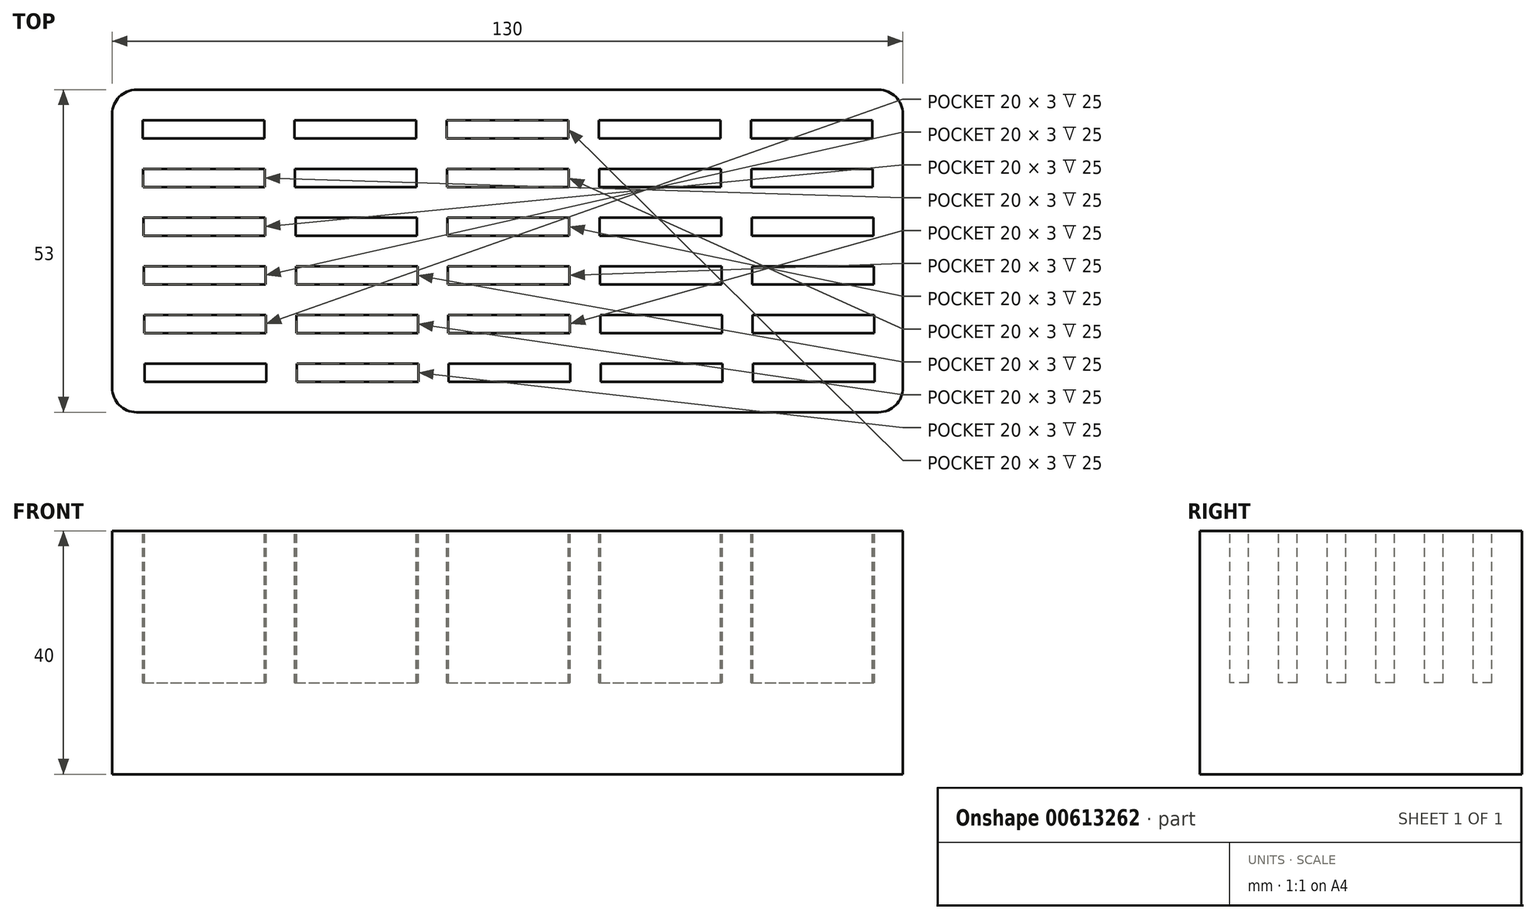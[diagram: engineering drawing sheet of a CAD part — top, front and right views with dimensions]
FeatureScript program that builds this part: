
annotation { "Feature Type Name" : "Feature", "Feature Type Description" : "" }
export const myFeature = defineFeature(function(context is Context, id is Id, definition is map)
    precondition{}
    {
        {
            var Q0;
            Q0=qCreatedBy(makeId("Top.planeOp"),FACE);
            var sketch = newSketch(context, id + "F0", { "sketchPlane" : qUnion([Q0])});
            skLineSegment(sketch, "E0.bottom", {"start": v(4, 0) * mm, "end": v(126, 0) * mm});
            skLineSegment(sketch, "E0.top", {"start": v(4, 53) * mm, "end": v(126, 53) * mm});
            skLineSegment(sketch, "E0.left", {"start": v(0, 4) * mm, "end": v(0, 49) * mm});
            skLineSegment(sketch, "E0.right", {"start": v(130, 4) * mm, "end": v(130, 49) * mm});
            skPoint(sketch, "E1.visualSharp", {"position": v(0, 53) * mm});
            skArc(sketch, "E1.filletArc", {"start": v(4, 53) * mm, "mid": v(1.17, 51.83) * mm, "end": v(0, 49) * mm});
            skPoint(sketch, "E2.visualSharp", {"position": v(0, 0) * mm});
            skArc(sketch, "E2.filletArc", {"start": v(0, 4) * mm, "mid": v(1.17, 1.17) * mm, "end": v(4, 0) * mm});
            skPoint(sketch, "E3.visualSharp", {"position": v(130, 0) * mm});
            skArc(sketch, "E3.filletArc", {"start": v(126, 0) * mm, "mid": v(128.83, 1.17) * mm, "end": v(130, 4) * mm});
            skPoint(sketch, "E4.visualSharp", {"position": v(130, 53) * mm});
            skArc(sketch, "E4.filletArc", {"start": v(130, 49) * mm, "mid": v(128.83, 51.83) * mm, "end": v(126, 53) * mm});
            skSolve(sketch);
        }
        {
            var Q0;
            Q0 = qSketchRegion(id + "F0", true);
            extrude(context, id + "F1", {"entities" : qUnion([Q0]), "depth" : 40 * mm, "offsetDistance" : 25.4 * mm});
        }
        {
            var Q0;
            Q0=makeQuery(id+"F1.opExtrude","CAP_FACE",FACE,{"disambiguationData":[OSD([sQuery(id+"F0.wireOp",EDGE,"E0.bottom"),sQuery(id+"F0.wireOp",EDGE,"E0.top"),sQuery(id+"F0.wireOp",EDGE,"E0.left"),sQuery(id+"F0.wireOp",EDGE,"E0.right"),sQuery(id+"F0.wireOp",EDGE,"E1.filletArc"),sQuery(id+"F0.wireOp",EDGE,"E2.filletArc"),sQuery(id+"F0.wireOp",EDGE,"E3.filletArc"),sQuery(id+"F0.wireOp",EDGE,"E4.filletArc")])],"isStart":false});
            var sketch = newSketch(context, id + "F2", { "sketchPlane" : qUnion([Q0])});
            skLineSegment(sketch, "E5.bottom", {"start": v(5, 48) * mm, "end": v(25, 48) * mm});
            skLineSegment(sketch, "E5.top", {"start": v(5, 45) * mm, "end": v(25, 45) * mm});
            skLineSegment(sketch, "E5.left", {"start": v(5, 48) * mm, "end": v(5, 45) * mm});
            skLineSegment(sketch, "E5.right", {"start": v(25, 48) * mm, "end": v(25, 45) * mm});
            skLineSegment(sketch, "E6.0.1.0", {"start": v(5.07, 37) * mm, "end": v(25.07, 37) * mm});
            skLineSegment(sketch, "E6.0.1.1", {"start": v(5.07, 40) * mm, "end": v(25.07, 40) * mm});
            skLineSegment(sketch, "E6.0.1.2", {"start": v(25.07, 40) * mm, "end": v(25.07, 37) * mm});
            skLineSegment(sketch, "E6.0.1.3", {"start": v(5.07, 40) * mm, "end": v(5.07, 37) * mm});
            skLineSegment(sketch, "E6.0.2.0", {"start": v(5.13, 29) * mm, "end": v(25.13, 29) * mm});
            skLineSegment(sketch, "E6.0.2.1", {"start": v(5.13, 32) * mm, "end": v(25.13, 32) * mm});
            skLineSegment(sketch, "E6.0.2.2", {"start": v(25.13, 32) * mm, "end": v(25.13, 29) * mm});
            skLineSegment(sketch, "E6.0.2.3", {"start": v(5.13, 32) * mm, "end": v(5.13, 29) * mm});
            skLineSegment(sketch, "E6.0.3.0", {"start": v(5.2, 21) * mm, "end": v(25.2, 21) * mm});
            skLineSegment(sketch, "E6.0.3.1", {"start": v(5.2, 24) * mm, "end": v(25.2, 24) * mm});
            skLineSegment(sketch, "E6.0.3.2", {"start": v(25.2, 24) * mm, "end": v(25.2, 21) * mm});
            skLineSegment(sketch, "E6.0.3.3", {"start": v(5.2, 24) * mm, "end": v(5.2, 21) * mm});
            skLineSegment(sketch, "E6.0.4.0", {"start": v(5.27, 13) * mm, "end": v(25.27, 13) * mm});
            skLineSegment(sketch, "E6.0.4.1", {"start": v(5.27, 16) * mm, "end": v(25.27, 16) * mm});
            skLineSegment(sketch, "E6.0.4.2", {"start": v(25.27, 16) * mm, "end": v(25.27, 13) * mm});
            skLineSegment(sketch, "E6.0.4.3", {"start": v(5.27, 16) * mm, "end": v(5.27, 13) * mm});
            skLineSegment(sketch, "E6.0.5.0", {"start": v(5.33, 5) * mm, "end": v(25.33, 5) * mm});
            skLineSegment(sketch, "E6.0.5.1", {"start": v(5.33, 8) * mm, "end": v(25.33, 8) * mm});
            skLineSegment(sketch, "E6.0.5.2", {"start": v(25.33, 8) * mm, "end": v(25.33, 5) * mm});
            skLineSegment(sketch, "E6.0.5.3", {"start": v(5.33, 8) * mm, "end": v(5.33, 5) * mm});
            skLineSegment(sketch, "E6.1.0.0", {"start": v(30, 45) * mm, "end": v(50, 45) * mm});
            skLineSegment(sketch, "E6.1.0.1", {"start": v(30, 48) * mm, "end": v(50, 48) * mm});
            skLineSegment(sketch, "E6.1.0.2", {"start": v(50, 48) * mm, "end": v(50, 45) * mm});
            skLineSegment(sketch, "E6.1.0.3", {"start": v(30, 48) * mm, "end": v(30, 45) * mm});
            skLineSegment(sketch, "E6.1.1.0", {"start": v(30.07, 37) * mm, "end": v(50.07, 37) * mm});
            skLineSegment(sketch, "E6.1.1.1", {"start": v(30.07, 40) * mm, "end": v(50.07, 40) * mm});
            skLineSegment(sketch, "E6.1.1.2", {"start": v(50.07, 40) * mm, "end": v(50.07, 37) * mm});
            skLineSegment(sketch, "E6.1.1.3", {"start": v(30.07, 40) * mm, "end": v(30.07, 37) * mm});
            skLineSegment(sketch, "E6.1.2.0", {"start": v(30.13, 29) * mm, "end": v(50.13, 29) * mm});
            skLineSegment(sketch, "E6.1.2.1", {"start": v(30.13, 32) * mm, "end": v(50.13, 32) * mm});
            skLineSegment(sketch, "E6.1.2.2", {"start": v(50.13, 32) * mm, "end": v(50.13, 29) * mm});
            skLineSegment(sketch, "E6.1.2.3", {"start": v(30.13, 32) * mm, "end": v(30.13, 29) * mm});
            skLineSegment(sketch, "E6.1.3.0", {"start": v(30.2, 21) * mm, "end": v(50.2, 21) * mm});
            skLineSegment(sketch, "E6.1.3.1", {"start": v(30.2, 24) * mm, "end": v(50.2, 24) * mm});
            skLineSegment(sketch, "E6.1.3.2", {"start": v(50.2, 24) * mm, "end": v(50.2, 21) * mm});
            skLineSegment(sketch, "E6.1.3.3", {"start": v(30.2, 24) * mm, "end": v(30.2, 21) * mm});
            skLineSegment(sketch, "E6.1.4.0", {"start": v(30.27, 13) * mm, "end": v(50.27, 13) * mm});
            skLineSegment(sketch, "E6.1.4.1", {"start": v(30.27, 16) * mm, "end": v(50.27, 16) * mm});
            skLineSegment(sketch, "E6.1.4.2", {"start": v(50.27, 16) * mm, "end": v(50.27, 13) * mm});
            skLineSegment(sketch, "E6.1.4.3", {"start": v(30.27, 16) * mm, "end": v(30.27, 13) * mm});
            skLineSegment(sketch, "E6.1.5.0", {"start": v(30.33, 5) * mm, "end": v(50.33, 5) * mm});
            skLineSegment(sketch, "E6.1.5.1", {"start": v(30.33, 8) * mm, "end": v(50.33, 8) * mm});
            skLineSegment(sketch, "E6.1.5.2", {"start": v(50.33, 8) * mm, "end": v(50.33, 5) * mm});
            skLineSegment(sketch, "E6.1.5.3", {"start": v(30.33, 8) * mm, "end": v(30.33, 5) * mm});
            skLineSegment(sketch, "E6.2.0.0", {"start": v(55, 45) * mm, "end": v(75, 45) * mm});
            skLineSegment(sketch, "E6.2.0.1", {"start": v(55, 48) * mm, "end": v(75, 48) * mm});
            skLineSegment(sketch, "E6.2.0.2", {"start": v(75, 48) * mm, "end": v(75, 45) * mm});
            skLineSegment(sketch, "E6.2.0.3", {"start": v(55, 48) * mm, "end": v(55, 45) * mm});
            skLineSegment(sketch, "E6.2.1.0", {"start": v(55.07, 37) * mm, "end": v(75.07, 37) * mm});
            skLineSegment(sketch, "E6.2.1.1", {"start": v(55.07, 40) * mm, "end": v(75.07, 40) * mm});
            skLineSegment(sketch, "E6.2.1.2", {"start": v(75.07, 40) * mm, "end": v(75.07, 37) * mm});
            skLineSegment(sketch, "E6.2.1.3", {"start": v(55.07, 40) * mm, "end": v(55.07, 37) * mm});
            skLineSegment(sketch, "E6.2.2.0", {"start": v(55.13, 29) * mm, "end": v(75.13, 29) * mm});
            skLineSegment(sketch, "E6.2.2.1", {"start": v(55.13, 32) * mm, "end": v(75.13, 32) * mm});
            skLineSegment(sketch, "E6.2.2.2", {"start": v(75.13, 32) * mm, "end": v(75.13, 29) * mm});
            skLineSegment(sketch, "E6.2.2.3", {"start": v(55.13, 32) * mm, "end": v(55.13, 29) * mm});
            skLineSegment(sketch, "E6.2.3.0", {"start": v(55.2, 21) * mm, "end": v(75.2, 21) * mm});
            skLineSegment(sketch, "E6.2.3.1", {"start": v(55.2, 24) * mm, "end": v(75.2, 24) * mm});
            skLineSegment(sketch, "E6.2.3.2", {"start": v(75.2, 24) * mm, "end": v(75.2, 21) * mm});
            skLineSegment(sketch, "E6.2.3.3", {"start": v(55.2, 24) * mm, "end": v(55.2, 21) * mm});
            skLineSegment(sketch, "E6.2.4.0", {"start": v(55.27, 13) * mm, "end": v(75.27, 13) * mm});
            skLineSegment(sketch, "E6.2.4.1", {"start": v(55.27, 16) * mm, "end": v(75.27, 16) * mm});
            skLineSegment(sketch, "E6.2.4.2", {"start": v(75.27, 16) * mm, "end": v(75.27, 13) * mm});
            skLineSegment(sketch, "E6.2.4.3", {"start": v(55.27, 16) * mm, "end": v(55.27, 13) * mm});
            skLineSegment(sketch, "E6.2.5.0", {"start": v(55.33, 5) * mm, "end": v(75.33, 5) * mm});
            skLineSegment(sketch, "E6.2.5.1", {"start": v(55.33, 8) * mm, "end": v(75.33, 8) * mm});
            skLineSegment(sketch, "E6.2.5.2", {"start": v(75.33, 8) * mm, "end": v(75.33, 5) * mm});
            skLineSegment(sketch, "E6.2.5.3", {"start": v(55.33, 8) * mm, "end": v(55.33, 5) * mm});
            skLineSegment(sketch, "E6.3.0.0", {"start": v(80, 45) * mm, "end": v(100, 45) * mm});
            skLineSegment(sketch, "E6.3.0.1", {"start": v(80, 48) * mm, "end": v(100, 48) * mm});
            skLineSegment(sketch, "E6.3.0.2", {"start": v(100, 48) * mm, "end": v(100, 45) * mm});
            skLineSegment(sketch, "E6.3.0.3", {"start": v(80, 48) * mm, "end": v(80, 45) * mm});
            skLineSegment(sketch, "E6.3.1.0", {"start": v(80.07, 37) * mm, "end": v(100.07, 37) * mm});
            skLineSegment(sketch, "E6.3.1.1", {"start": v(80.07, 40) * mm, "end": v(100.07, 40) * mm});
            skLineSegment(sketch, "E6.3.1.2", {"start": v(100.07, 40) * mm, "end": v(100.07, 37) * mm});
            skLineSegment(sketch, "E6.3.1.3", {"start": v(80.07, 40) * mm, "end": v(80.07, 37) * mm});
            skLineSegment(sketch, "E6.3.2.0", {"start": v(80.13, 29) * mm, "end": v(100.13, 29) * mm});
            skLineSegment(sketch, "E6.3.2.1", {"start": v(80.13, 32) * mm, "end": v(100.13, 32) * mm});
            skLineSegment(sketch, "E6.3.2.2", {"start": v(100.13, 32) * mm, "end": v(100.13, 29) * mm});
            skLineSegment(sketch, "E6.3.2.3", {"start": v(80.13, 32) * mm, "end": v(80.13, 29) * mm});
            skLineSegment(sketch, "E6.3.3.0", {"start": v(80.2, 21) * mm, "end": v(100.2, 21) * mm});
            skLineSegment(sketch, "E6.3.3.1", {"start": v(80.2, 24) * mm, "end": v(100.2, 24) * mm});
            skLineSegment(sketch, "E6.3.3.2", {"start": v(100.2, 24) * mm, "end": v(100.2, 21) * mm});
            skLineSegment(sketch, "E6.3.3.3", {"start": v(80.2, 24) * mm, "end": v(80.2, 21) * mm});
            skLineSegment(sketch, "E6.3.4.0", {"start": v(80.27, 13) * mm, "end": v(100.27, 13) * mm});
            skLineSegment(sketch, "E6.3.4.1", {"start": v(80.27, 16) * mm, "end": v(100.27, 16) * mm});
            skLineSegment(sketch, "E6.3.4.2", {"start": v(100.27, 16) * mm, "end": v(100.27, 13) * mm});
            skLineSegment(sketch, "E6.3.4.3", {"start": v(80.27, 16) * mm, "end": v(80.27, 13) * mm});
            skLineSegment(sketch, "E6.3.5.0", {"start": v(80.33, 5) * mm, "end": v(100.33, 5) * mm});
            skLineSegment(sketch, "E6.3.5.1", {"start": v(80.33, 8) * mm, "end": v(100.33, 8) * mm});
            skLineSegment(sketch, "E6.3.5.2", {"start": v(100.33, 8) * mm, "end": v(100.33, 5) * mm});
            skLineSegment(sketch, "E6.3.5.3", {"start": v(80.33, 8) * mm, "end": v(80.33, 5) * mm});
            skLineSegment(sketch, "E6.4.0.0", {"start": v(105, 45) * mm, "end": v(125, 45) * mm});
            skLineSegment(sketch, "E6.4.0.1", {"start": v(105, 48) * mm, "end": v(125, 48) * mm});
            skLineSegment(sketch, "E6.4.0.2", {"start": v(125, 48) * mm, "end": v(125, 45) * mm});
            skLineSegment(sketch, "E6.4.0.3", {"start": v(105, 48) * mm, "end": v(105, 45) * mm});
            skLineSegment(sketch, "E6.4.1.0", {"start": v(105.07, 37) * mm, "end": v(125.07, 37) * mm});
            skLineSegment(sketch, "E6.4.1.1", {"start": v(105.07, 40) * mm, "end": v(125.07, 40) * mm});
            skLineSegment(sketch, "E6.4.1.2", {"start": v(125.07, 40) * mm, "end": v(125.07, 37) * mm});
            skLineSegment(sketch, "E6.4.1.3", {"start": v(105.07, 40) * mm, "end": v(105.07, 37) * mm});
            skLineSegment(sketch, "E6.4.2.0", {"start": v(105.13, 29) * mm, "end": v(125.13, 29) * mm});
            skLineSegment(sketch, "E6.4.2.1", {"start": v(105.13, 32) * mm, "end": v(125.13, 32) * mm});
            skLineSegment(sketch, "E6.4.2.2", {"start": v(125.13, 32) * mm, "end": v(125.13, 29) * mm});
            skLineSegment(sketch, "E6.4.2.3", {"start": v(105.13, 32) * mm, "end": v(105.13, 29) * mm});
            skLineSegment(sketch, "E6.4.3.0", {"start": v(105.2, 21) * mm, "end": v(125.2, 21) * mm});
            skLineSegment(sketch, "E6.4.3.1", {"start": v(105.2, 24) * mm, "end": v(125.2, 24) * mm});
            skLineSegment(sketch, "E6.4.3.2", {"start": v(125.2, 24) * mm, "end": v(125.2, 21) * mm});
            skLineSegment(sketch, "E6.4.3.3", {"start": v(105.2, 24) * mm, "end": v(105.2, 21) * mm});
            skLineSegment(sketch, "E6.4.4.0", {"start": v(105.27, 13) * mm, "end": v(125.27, 13) * mm});
            skLineSegment(sketch, "E6.4.4.1", {"start": v(105.27, 16) * mm, "end": v(125.27, 16) * mm});
            skLineSegment(sketch, "E6.4.4.2", {"start": v(125.27, 16) * mm, "end": v(125.27, 13) * mm});
            skLineSegment(sketch, "E6.4.4.3", {"start": v(105.27, 16) * mm, "end": v(105.27, 13) * mm});
            skLineSegment(sketch, "E6.4.5.0", {"start": v(105.33, 5) * mm, "end": v(125.33, 5) * mm});
            skLineSegment(sketch, "E6.4.5.1", {"start": v(105.33, 8) * mm, "end": v(125.33, 8) * mm});
            skLineSegment(sketch, "E6.4.5.2", {"start": v(125.33, 8) * mm, "end": v(125.33, 5) * mm});
            skLineSegment(sketch, "E6.4.5.3", {"start": v(105.33, 8) * mm, "end": v(105.33, 5) * mm});
            skLineSegment(sketch, "E6.direction1", {"start": v(5, 45) * mm, "end": v(30, 45) * mm, "construction": true});
            skLineSegment(sketch, "E6.direction2", {"start": v(5, 45) * mm, "end": v(5.07, 37) * mm, "construction": true});
            skSolve(sketch);
        }
        {
            var Q0;
            Q0 = qSketchRegion(id + "F2", true);
            extrude(context, id + "F3", {"entities" : qUnion([Q0]), "operationType" : NewBodyOperationType.REMOVE, "oppositeDirection" : true, "depth" : 25 * mm, "offsetDistance" : 25.4 * mm});
        }
    });
